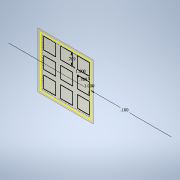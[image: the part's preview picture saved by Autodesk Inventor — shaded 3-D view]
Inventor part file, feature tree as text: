
AUTODESK INVENTOR PART (.ipt)
format: ipt  version: 2022 (Build 260153000, 153)  size: 107,008 bytes
history: native  units: in
note: dims shown in document units (in); Inventor stores cm internally (conversion verified against a paired STEP export)
features: other x2, plane x1, sketch x1, reference x1
ambient origin geometry x8: Origin, YZ Plane, XZ Plane, XY Plane, X Axis, Y Axis, Z Axis, Center Point
feature tree (5):
  plane  "Work Plane1"
  sketch  "Sketch1"  dims[d0=0.1in d1=0.7087in d2=0.7087in d3=1.1811in d5=1.0in d6=1.1811in d8=1.0in]
  reference  "Reference1"
  other  "Assembly1"
  other  "Stock 3x3x1.5:1"
